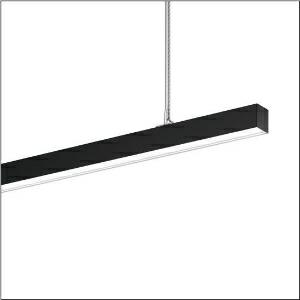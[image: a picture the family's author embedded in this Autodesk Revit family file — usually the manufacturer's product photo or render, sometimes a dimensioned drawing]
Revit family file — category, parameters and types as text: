
# Revit family: silica_r__21_51mx33dp3cbb_3ef4
name_source: partatom
category: Lighting Fixtures
units: mm (PartAtom-declared; Revit-internal decimal feet)

## family parameters
Cut with Voids When Loaded = No
Host = Face
Light Source = No
Part Type = Normal
Room Calculation Point = No
Round Connector Dimension = Use Diameter
Shared = No

## types (1)
- --- (1 x LED, 16260 lm, 109.1 W, 3000K)
    Apparent Load = 109 VA
    CIE Flux Codes = 78 96 99 55 100
    Color Rendering = 80
    Color Temperature = 3000K
    Default Elevation = 1800 mm
    Description = Silica® 21, office luminaire, primary optical cover: prismatic diffuser, of PMMA, CAT 2 (L<= 3000cd/m²), light emission: direct/indirect distribution, primary light characteristic: symmetric, installation type: suspended mounting, LED, rated luminous flux: 16.260lm, luminous efficacy: 149lm/W, light colour: 830, colour temperature: 3000K, control gear: DALI 2, with terminal, 3+2-pole, max. 2.5mm², mains connection: 220..240V, AC, 50/60Hz, rated input power: 109.1W, luminaire housing, of aluminium, matt jet black (RAL 9005), length: 3.300mm, width: 53mm, height: 53mm, protection rating (complete): IP20, insulation class (complete): insulation class I (protective earthing), certification: CE, permissible operating ambient temperature: 0..+35°C, standard: EN 50419, packaging unit: 1 piece
    Height = 53 mm
    Lamp = 1 x LED
    Lamp Light Flux = 16260 lm
    Lamp Power = 109.1 W
    Lamp count = 1
    Length = 3304 mm
    Luminous efficacy = 149 lm/W
    Manufacturer = Siteco
    ModVariant = No
    Model = 51MX33DP3CBB
    Mounting Place = Ceiling
    Mounting Type = Pendant
    Number of Poles = 1
    OnlyDefault = Yes
    Power Factor = 1
    Product Name = Silica® 21
    Product group = office luminaire | ceiling pendant
    ProductGroupID = 903
    Protection Class = Protection class I
    Protection Degree = IP 20
    RLX_Detail_Level = 1
    RLX_Emergency_Light_Flux = 0 lm
    RLX_Emergency_Type = 0
    RLX_Emergency_Type_DB = No
    RlxData = <blob elided: 25185 chars, md5=dc8d8e7d>
    Socket = socket
    Standby Power = 0 W
    System Light Flux = 16260 lm
    System Power = 109 W
    Type Comments = factory setting: luminous flux: 100 % | dim-lin: 254 | 344 mA
    Type Image = l_1335856.jpg
    URL = http://relux.com
    VarID = @adj_062063
    Voltage = 0 V
    Weight = 0.00 kg
    Width = 53 mm

## geometry (parser evidence)
native form markers: Blend x4, Sweep x16
no freeform markers — native parametric forms only
